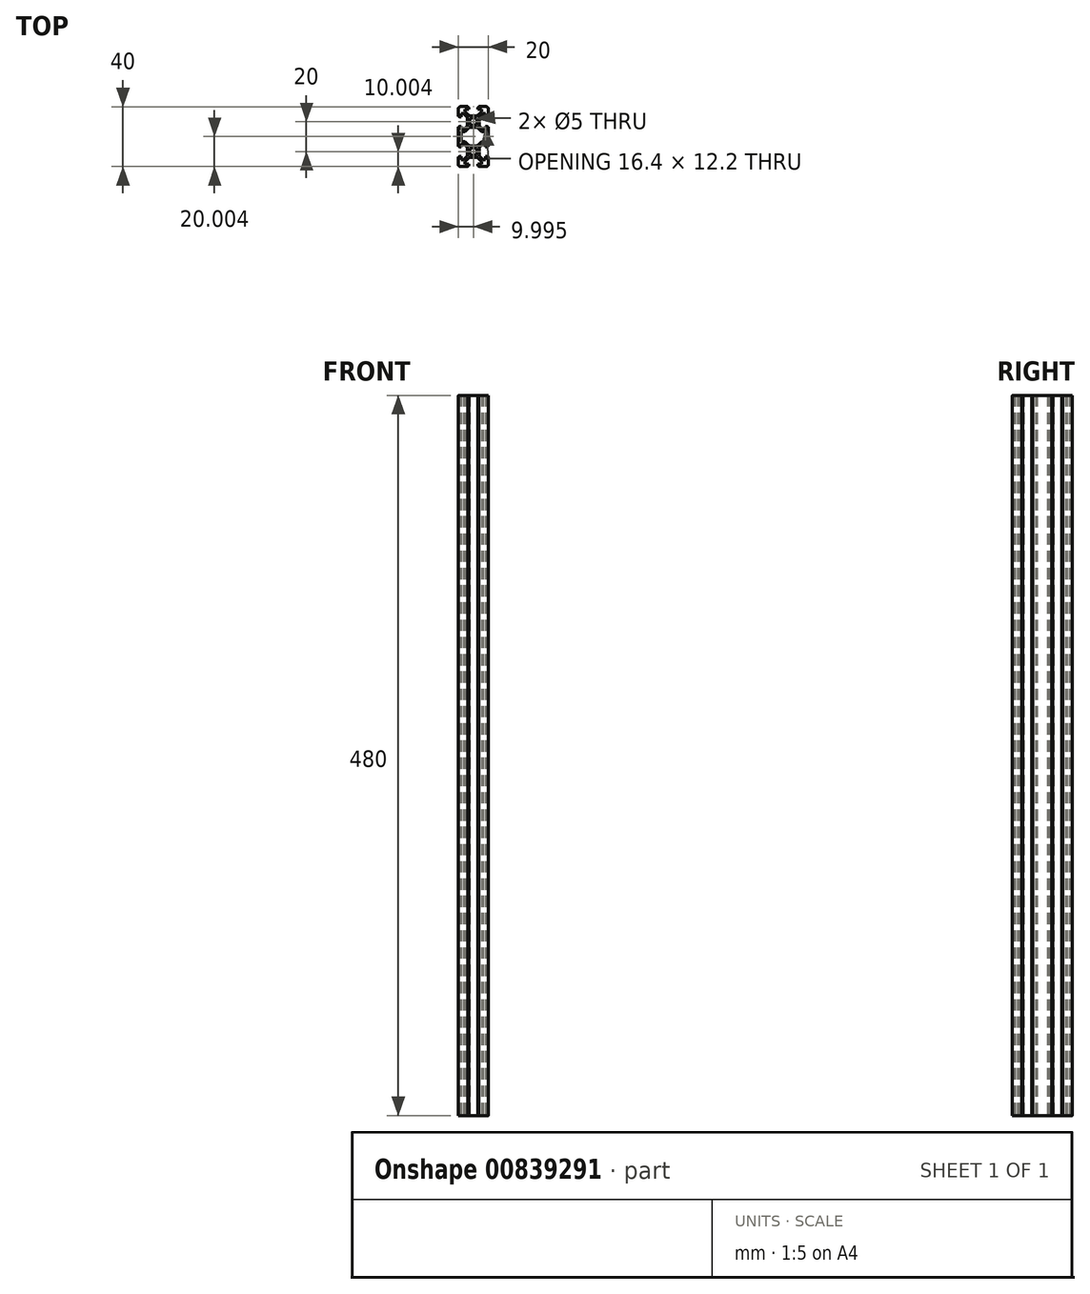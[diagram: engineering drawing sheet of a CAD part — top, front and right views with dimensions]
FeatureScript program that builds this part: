
annotation { "Feature Type Name" : "Feature", "Feature Type Description" : "" }
export const myFeature = defineFeature(function(context is Context, id is Id, definition is map)
    precondition{}
    {
        {
            var Q0;
            Q0=qCreatedBy(makeId("Top.planeOp"),FACE);
            var sketch = newSketch(context, id + "F0", { "sketchPlane" : qUnion([Q0])});
            skCircle(sketch, "E0", {"center": v(-160.4, -45.54) * mm, "radius": 2.5 * mm});
            skLineSegment(sketch, "E1.bottom", {"start": v(-151.9, -55.54) * mm, "end": v(-156.3, -55.54) * mm});
            skLineSegment(sketch, "E1.left", {"start": v(-150.4, -54.04) * mm, "end": v(-150.4, -49.14) * mm});
            skLineSegment(sketch, "E2.bottom", {"start": v(-158.38, -49.44) * mm, "end": v(-162.4, -49.44) * mm});
            skLineSegment(sketch, "E2.top", {"start": v(-158.38, -41.64) * mm, "end": v(-162.4, -41.64) * mm});
            skLineSegment(sketch, "E2.left", {"start": v(-156.5, -47.55) * mm, "end": v(-156.5, -43.52) * mm});
            skLineSegment(sketch, "E2.right", {"start": v(-164.3, -47.55) * mm, "end": v(-164.3, -43.52) * mm});
            skLineSegment(sketch, "E3.left", {"start": v(-150.4, -37.04) * mm, "end": v(-150.4, -40.04) * mm});
            skLineSegment(sketch, "E4", {"start": v(-155.9, -42.11) * mm, "end": v(-153.83, -40.04) * mm});
            skLineSegment(sketch, "E5.MirrorCS", {"start": v(-156.97, -41.05) * mm, "end": v(-154.9, -38.98) * mm});
            skLineSegment(sketch, "E6", {"start": v(-152.2, -40.04) * mm, "end": v(-152.2, -42.44) * mm});
            skLineSegment(sketch, "E7", {"start": v(-150.7, -41.94) * mm, "end": v(-150.4, -41.94) * mm});
            skLineSegment(sketch, "E8", {"start": v(-152.2, -42.44) * mm, "end": v(-150.9, -42.44) * mm});
            skLineSegment(sketch, "E9", {"start": v(-150.9, -42.14) * mm, "end": v(-150.9, -42.44) * mm});
            skPoint(sketch, "E10.visualSharp", {"position": v(-150.9, -41.94) * mm});
            skArc(sketch, "E10.filletArc", {"start": v(-150.7, -41.94) * mm, "mid": v(-150.84, -42) * mm, "end": v(-150.9, -42.14) * mm});
            skPoint(sketch, "E11.newPointA", {"position": v(-156.5, -42.7) * mm});
            skArc(sketch, "E11.filletArc", {"start": v(-155.9, -42.11) * mm, "mid": v(-156.34, -42.76) * mm, "end": v(-156.5, -43.52) * mm});
            skPoint(sketch, "E12.newPointA", {"position": v(-157.56, -41.64) * mm});
            skPoint(sketch, "E12.newPointB", {"position": v(-156.5, -41.64) * mm});
            skArc(sketch, "E12.filletArc", {"start": v(-158.38, -41.64) * mm, "mid": v(-157.62, -41.48) * mm, "end": v(-156.97, -41.05) * mm});
            skLineSegment(sketch, "E13.trimOffspring", {"start": v(-152.2, -40.04) * mm, "end": v(-153.83, -40.04) * mm});
            skLineSegment(sketch, "E14.MirrorCS", {"start": v(-150.7, -49.14) * mm, "end": v(-150.4, -49.14) * mm});
            skArc(sketch, "E15.MirrorCS", {"start": v(-150.7, -49.14) * mm, "mid": v(-150.84, -49.08) * mm, "end": v(-150.9, -48.94) * mm});
            skLineSegment(sketch, "E16.MirrorCS", {"start": v(-150.9, -48.94) * mm, "end": v(-150.9, -48.64) * mm});
            skArc(sketch, "E17.MirrorCS", {"start": v(-155.9, -48.96) * mm, "mid": v(-156.34, -48.31) * mm, "end": v(-156.5, -47.55) * mm});
            skLineSegment(sketch, "E18.MirrorCS", {"start": v(-152.2, -51.04) * mm, "end": v(-153.83, -51.04) * mm});
            skLineSegment(sketch, "E19.MirrorCS", {"start": v(-152.2, -48.64) * mm, "end": v(-150.9, -48.64) * mm});
            skLineSegment(sketch, "E20.MirrorCS", {"start": v(-151.9, -55.54) * mm, "end": v(-154.9, -55.54) * mm});
            skPoint(sketch, "E21.MirrorP", {"position": v(-150.9, -49.14) * mm});
            skLineSegment(sketch, "E22.MirrorCS", {"start": v(-157.3, -53.74) * mm, "end": v(-157.3, -55.04) * mm});
            skLineSegment(sketch, "E23.MirrorCS", {"start": v(-154.9, -53.74) * mm, "end": v(-157.3, -53.74) * mm});
            skLineSegment(sketch, "E24.MirrorCS", {"start": v(-152.2, -51.04) * mm, "end": v(-152.2, -48.64) * mm});
            skLineSegment(sketch, "E25.MirrorCS", {"start": v(-150.4, -54.04) * mm, "end": v(-150.4, -51.04) * mm});
            skLineSegment(sketch, "E26.MirrorCS", {"start": v(-155.9, -48.96) * mm, "end": v(-153.83, -51.04) * mm});
            skPoint(sketch, "E27.MirrorP", {"position": v(-156.5, -48.38) * mm});
            skPoint(sketch, "E28.MirrorP", {"position": v(-150.4, -55.54) * mm});
            skPoint(sketch, "E29.MirrorP", {"position": v(-156.5, -49.44) * mm});
            skLineSegment(sketch, "E30.MirrorCS", {"start": v(-156.97, -50.02) * mm, "end": v(-154.9, -52.1) * mm});
            skPoint(sketch, "E31.MirrorP", {"position": v(-157.56, -49.44) * mm});
            skArc(sketch, "E32.MirrorCS", {"start": v(-150.4, -54.04) * mm, "mid": v(-150.83, -55.1) * mm, "end": v(-151.9, -55.54) * mm});
            skLineSegment(sketch, "E33.MirrorCS", {"start": v(-154.9, -53.74) * mm, "end": v(-154.9, -52.1) * mm});
            skArc(sketch, "E34.MirrorCS", {"start": v(-158.38, -49.44) * mm, "mid": v(-157.62, -49.59) * mm, "end": v(-156.97, -50.02) * mm});
            skLineSegment(sketch, "E35.trimOffspring", {"start": v(-150.4, -41.94) * mm, "end": v(-150.4, -37.04) * mm});
            skLineSegment(sketch, "E36.MirrorCS", {"start": v(-156.8, -55.24) * mm, "end": v(-156.8, -55.54) * mm});
            skLineSegment(sketch, "E37.MirrorCS", {"start": v(-157, -55.04) * mm, "end": v(-157.3, -55.04) * mm});
            skLineSegment(sketch, "E38.MirrorCS", {"start": v(-156.3, -55.54) * mm, "end": v(-156.8, -55.54) * mm});
            skArc(sketch, "E39.MirrorCS", {"start": v(-156.8, -55.24) * mm, "mid": v(-156.85, -55.1) * mm, "end": v(-157, -55.04) * mm});
            skArc(sketch, "E40.MirrorCS", {"start": v(-170.1, -49.14) * mm, "mid": v(-169.95, -49.08) * mm, "end": v(-169.9, -48.94) * mm});
            skLineSegment(sketch, "E41.MirrorCS", {"start": v(-170.1, -41.94) * mm, "end": v(-170.4, -41.94) * mm});
            skLineSegment(sketch, "E42.MirrorCS", {"start": v(-169.9, -48.94) * mm, "end": v(-169.9, -48.64) * mm});
            skArc(sketch, "E43.MirrorCS", {"start": v(-170.1, -41.94) * mm, "mid": v(-169.95, -42) * mm, "end": v(-169.9, -42.14) * mm});
            skLineSegment(sketch, "E44.MirrorCS", {"start": v(-169.9, -42.14) * mm, "end": v(-169.9, -42.44) * mm});
            skLineSegment(sketch, "E45.MirrorCS", {"start": v(-170.1, -49.14) * mm, "end": v(-170.4, -49.14) * mm});
            skArc(sketch, "E46.MirrorCS", {"start": v(-170.4, -54.04) * mm, "mid": v(-169.96, -55.1) * mm, "end": v(-168.9, -55.54) * mm});
            skArc(sketch, "E47.MirrorCS", {"start": v(-164.88, -42.11) * mm, "mid": v(-164.45, -42.76) * mm, "end": v(-164.3, -43.52) * mm});
            skLineSegment(sketch, "E48.MirrorCS", {"start": v(-163.8, -55.04) * mm, "end": v(-163.5, -55.04) * mm});
            skLineSegment(sketch, "E49.MirrorCS", {"start": v(-162.4, -41.64) * mm, "end": v(-158.38, -41.64) * mm});
            skLineSegment(sketch, "E50.MirrorCS", {"start": v(-168.6, -48.64) * mm, "end": v(-169.9, -48.64) * mm});
            skLineSegment(sketch, "E51.MirrorCS", {"start": v(-168.6, -42.44) * mm, "end": v(-169.9, -42.44) * mm});
            skArc(sketch, "E52.MirrorCS", {"start": v(-164.88, -48.96) * mm, "mid": v(-164.45, -48.31) * mm, "end": v(-164.3, -47.55) * mm});
            skArc(sketch, "E53.MirrorCS", {"start": v(-164, -55.24) * mm, "mid": v(-163.94, -55.1) * mm, "end": v(-163.8, -55.04) * mm});
            skLineSegment(sketch, "E54.MirrorCS", {"start": v(-164, -55.24) * mm, "end": v(-164, -55.54) * mm});
            skLineSegment(sketch, "E55.MirrorCS", {"start": v(-162.4, -49.44) * mm, "end": v(-158.38, -49.44) * mm});
            skLineSegment(sketch, "E56.MirrorCS", {"start": v(-164.5, -55.54) * mm, "end": v(-164, -55.54) * mm});
            skLineSegment(sketch, "E57.MirrorCS", {"start": v(-163.5, -53.74) * mm, "end": v(-163.5, -55.04) * mm});
            skArc(sketch, "E58.MirrorCS", {"start": v(-162.4, -41.64) * mm, "mid": v(-163.17, -41.48) * mm, "end": v(-163.82, -41.05) * mm});
            skPoint(sketch, "E59.MirrorP", {"position": v(-170.4, -55.54) * mm});
            skLineSegment(sketch, "E60.MirrorCS", {"start": v(-168.9, -55.54) * mm, "end": v(-164.5, -55.54) * mm});
            skPoint(sketch, "E61.MirrorP", {"position": v(-164.3, -49.44) * mm});
            skArc(sketch, "E62.MirrorCS", {"start": v(-162.4, -49.44) * mm, "mid": v(-163.17, -49.59) * mm, "end": v(-163.82, -50.02) * mm});
            skPoint(sketch, "E63.MirrorP", {"position": v(-164.3, -48.38) * mm});
            skLineSegment(sketch, "E64.MirrorCS", {"start": v(-163.82, -41.05) * mm, "end": v(-165.9, -38.98) * mm});
            skPoint(sketch, "E65.MirrorP", {"position": v(-164.3, -42.7) * mm});
            skLineSegment(sketch, "E66.MirrorCS", {"start": v(-168.6, -51.04) * mm, "end": v(-168.6, -48.64) * mm});
            skLineSegment(sketch, "E67.MirrorCS", {"start": v(-164.88, -48.96) * mm, "end": v(-166.96, -51.04) * mm});
            skLineSegment(sketch, "E68.MirrorCS", {"start": v(-165.9, -53.74) * mm, "end": v(-163.5, -53.74) * mm});
            skLineSegment(sketch, "E69.MirrorCS", {"start": v(-168.6, -51.04) * mm, "end": v(-166.96, -51.04) * mm});
            skLineSegment(sketch, "E70.MirrorCS", {"start": v(-170.4, -54.04) * mm, "end": v(-170.4, -51.04) * mm});
            skLineSegment(sketch, "E71.MirrorCS", {"start": v(-170.4, -41.94) * mm, "end": v(-170.4, -37.04) * mm});
            skLineSegment(sketch, "E72.MirrorCS", {"start": v(-163.82, -50.02) * mm, "end": v(-165.9, -52.1) * mm});
            skPoint(sketch, "E73.MirrorP", {"position": v(-163.23, -49.44) * mm});
            skLineSegment(sketch, "E74.MirrorCS", {"start": v(-168.6, -40.04) * mm, "end": v(-168.6, -42.44) * mm});
            skLineSegment(sketch, "E75.MirrorCS", {"start": v(-170.4, -37.04) * mm, "end": v(-170.4, -40.04) * mm});
            skPoint(sketch, "E76.MirrorP", {"position": v(-169.9, -49.14) * mm});
            skPoint(sketch, "E77.MirrorP", {"position": v(-170.4, -35.54) * mm});
            skPoint(sketch, "E78.MirrorP", {"position": v(-169.9, -41.94) * mm});
            skLineSegment(sketch, "E79.MirrorCS", {"start": v(-164.88, -42.11) * mm, "end": v(-166.96, -40.04) * mm});
            skLineSegment(sketch, "E80.MirrorCS", {"start": v(-168.6, -40.04) * mm, "end": v(-166.96, -40.04) * mm});
            skLineSegment(sketch, "E81.MirrorCS", {"start": v(-170.4, -54.04) * mm, "end": v(-170.4, -49.14) * mm});
            skLineSegment(sketch, "E82.MirrorCS", {"start": v(-168.9, -55.54) * mm, "end": v(-165.9, -55.54) * mm});
            skPoint(sketch, "E83.MirrorP", {"position": v(-164.3, -41.64) * mm});
            skPoint(sketch, "E84.MirrorP", {"position": v(-163.23, -41.64) * mm});
            skLineSegment(sketch, "E85.MirrorCS", {"start": v(-165.9, -53.74) * mm, "end": v(-165.9, -52.1) * mm});
            skLineSegment(sketch, "E86", {"start": v(-168.6, -38.98) * mm, "end": v(-168.6, -35.54) * mm});
            skLineSegment(sketch, "E87", {"start": v(-170.4, -37.04) * mm, "end": v(-170.4, -35.54) * mm});
            skLineSegment(sketch, "E88", {"start": v(-150.4, -35.54) * mm, "end": v(-150.4, -37.04) * mm});
            skLineSegment(sketch, "E89", {"start": v(-152.2, -38.98) * mm, "end": v(-152.2, -35.54) * mm});
            skLineSegment(sketch, "E90", {"start": v(-154.9, -38.98) * mm, "end": v(-152.2, -38.98) * mm});
            skLineSegment(sketch, "E91", {"start": v(-165.9, -38.98) * mm, "end": v(-168.6, -38.98) * mm});
            skLineSegment(sketch, "E92.MirrorCS", {"start": v(-150.7, -21.94) * mm, "end": v(-150.4, -21.94) * mm});
            skLineSegment(sketch, "E93.MirrorCS", {"start": v(-150.9, -22.14) * mm, "end": v(-150.9, -22.44) * mm});
            skArc(sketch, "E94.MirrorCS", {"start": v(-150.7, -21.94) * mm, "mid": v(-150.84, -22) * mm, "end": v(-150.9, -22.14) * mm});
            skArc(sketch, "E95.MirrorCS", {"start": v(-150.7, -29.14) * mm, "mid": v(-150.84, -29.08) * mm, "end": v(-150.9, -28.94) * mm});
            skLineSegment(sketch, "E96.MirrorCS", {"start": v(-150.9, -28.94) * mm, "end": v(-150.9, -28.64) * mm});
            skLineSegment(sketch, "E97.MirrorCS", {"start": v(-169.9, -22.14) * mm, "end": v(-169.9, -22.44) * mm});
            skLineSegment(sketch, "E98.MirrorCS", {"start": v(-150.7, -29.14) * mm, "end": v(-150.4, -29.14) * mm});
            skArc(sketch, "E99.MirrorCS", {"start": v(-170.1, -21.94) * mm, "mid": v(-169.95, -22) * mm, "end": v(-169.9, -22.14) * mm});
            skLineSegment(sketch, "E100.MirrorCS", {"start": v(-170.1, -21.94) * mm, "end": v(-170.4, -21.94) * mm});
            skLineSegment(sketch, "E101.MirrorCS", {"start": v(-169.9, -28.94) * mm, "end": v(-169.9, -28.64) * mm});
            skArc(sketch, "E102.MirrorCS", {"start": v(-170.1, -29.14) * mm, "mid": v(-169.95, -29.08) * mm, "end": v(-169.9, -28.94) * mm});
            skLineSegment(sketch, "E103.MirrorCS", {"start": v(-170.1, -29.14) * mm, "end": v(-170.4, -29.14) * mm});
            skArc(sketch, "E104.MirrorCS", {"start": v(-158.38, -21.64) * mm, "mid": v(-157.62, -21.48) * mm, "end": v(-156.97, -21.05) * mm});
            skLineSegment(sketch, "E105.MirrorCS", {"start": v(-156.8, -15.84) * mm, "end": v(-156.8, -15.54) * mm});
            skArc(sketch, "E106.MirrorCS", {"start": v(-158.38, -29.44) * mm, "mid": v(-157.62, -29.59) * mm, "end": v(-156.97, -30.02) * mm});
            skLineSegment(sketch, "E107.MirrorCS", {"start": v(-152.2, -31.04) * mm, "end": v(-153.83, -31.04) * mm});
            skLineSegment(sketch, "E108.MirrorCS", {"start": v(-163.8, -16.04) * mm, "end": v(-163.5, -16.04) * mm});
            skLineSegment(sketch, "E109.MirrorCS", {"start": v(-168.6, -20.04) * mm, "end": v(-166.96, -20.04) * mm});
            skArc(sketch, "E110.MirrorCS", {"start": v(-170.4, -17.04) * mm, "mid": v(-169.96, -15.98) * mm, "end": v(-168.9, -15.54) * mm});
            skLineSegment(sketch, "E111.MirrorCS", {"start": v(-152.2, -28.64) * mm, "end": v(-150.9, -28.64) * mm});
            skLineSegment(sketch, "E112.MirrorCS", {"start": v(-164.5, -15.54) * mm, "end": v(-164, -15.54) * mm});
            skArc(sketch, "E113.MirrorCS", {"start": v(-164.88, -22.11) * mm, "mid": v(-164.45, -22.76) * mm, "end": v(-164.3, -23.52) * mm});
            skArc(sketch, "E114.MirrorCS", {"start": v(-150.4, -17.04) * mm, "mid": v(-150.83, -15.98) * mm, "end": v(-151.9, -15.54) * mm});
            skArc(sketch, "E115.MirrorCS", {"start": v(-162.4, -29.44) * mm, "mid": v(-163.17, -29.59) * mm, "end": v(-163.82, -30.02) * mm});
            skLineSegment(sketch, "E116.MirrorCS", {"start": v(-168.6, -22.44) * mm, "end": v(-169.9, -22.44) * mm});
            skLineSegment(sketch, "E117.MirrorCS", {"start": v(-164, -15.84) * mm, "end": v(-164, -15.54) * mm});
            skLineSegment(sketch, "E118.MirrorCS", {"start": v(-157.3, -17.34) * mm, "end": v(-157.3, -16.04) * mm});
            skLineSegment(sketch, "E119.MirrorCS", {"start": v(-156.3, -15.54) * mm, "end": v(-156.8, -15.54) * mm});
            skLineSegment(sketch, "E120.MirrorCS", {"start": v(-163.5, -17.34) * mm, "end": v(-163.5, -16.04) * mm});
            skArc(sketch, "E121.MirrorCS", {"start": v(-155.9, -28.96) * mm, "mid": v(-156.34, -28.31) * mm, "end": v(-156.5, -27.55) * mm});
            skArc(sketch, "E122.MirrorCS", {"start": v(-164.88, -28.96) * mm, "mid": v(-164.45, -28.31) * mm, "end": v(-164.3, -27.55) * mm});
            skLineSegment(sketch, "E123.MirrorCS", {"start": v(-152.2, -22.44) * mm, "end": v(-150.9, -22.44) * mm});
            skLineSegment(sketch, "E124.MirrorCS", {"start": v(-152.2, -20.04) * mm, "end": v(-153.83, -20.04) * mm});
            skArc(sketch, "E125.MirrorCS", {"start": v(-164, -15.84) * mm, "mid": v(-163.94, -15.98) * mm, "end": v(-163.8, -16.04) * mm});
            skLineSegment(sketch, "E126.MirrorCS", {"start": v(-157, -16.04) * mm, "end": v(-157.3, -16.04) * mm});
            skLineSegment(sketch, "E127.MirrorCS", {"start": v(-168.6, -31.04) * mm, "end": v(-166.96, -31.04) * mm});
            skLineSegment(sketch, "E128.MirrorCS", {"start": v(-168.6, -28.64) * mm, "end": v(-169.9, -28.64) * mm});
            skLineSegment(sketch, "E129.MirrorCS", {"start": v(-154.9, -17.34) * mm, "end": v(-154.9, -18.98) * mm});
            skLineSegment(sketch, "E130.MirrorCS", {"start": v(-165.9, -17.34) * mm, "end": v(-165.9, -18.98) * mm});
            skArc(sketch, "E131.MirrorCS", {"start": v(-162.4, -21.64) * mm, "mid": v(-163.17, -21.48) * mm, "end": v(-163.82, -21.05) * mm});
            skArc(sketch, "E132.MirrorCS", {"start": v(-155.9, -22.11) * mm, "mid": v(-156.34, -22.76) * mm, "end": v(-156.5, -23.52) * mm});
            skArc(sketch, "E133.MirrorCS", {"start": v(-156.8, -15.84) * mm, "mid": v(-156.85, -15.98) * mm, "end": v(-157, -16.04) * mm});
            skPoint(sketch, "E134.MirrorP", {"position": v(-160.4, -25.54) * mm});
            skLineSegment(sketch, "E135.MirrorCS", {"start": v(-164.3, -23.52) * mm, "end": v(-164.3, -27.55) * mm});
            skPoint(sketch, "E136.MirrorP", {"position": v(-164.3, -21.64) * mm});
            skLineSegment(sketch, "E137.MirrorCS", {"start": v(-151.9, -15.54) * mm, "end": v(-154.9, -15.54) * mm});
            skLineSegment(sketch, "E138.MirrorCS", {"start": v(-158.38, -29.44) * mm, "end": v(-162.4, -29.44) * mm});
            skLineSegment(sketch, "E139.MirrorCS", {"start": v(-170.4, -17.04) * mm, "end": v(-170.4, -21.94) * mm});
            skLineSegment(sketch, "E140.MirrorCS", {"start": v(-150.4, -34.04) * mm, "end": v(-150.4, -31.04) * mm});
            skPoint(sketch, "E141.MirrorP", {"position": v(-156.5, -21.64) * mm});
            skLineSegment(sketch, "E142.MirrorCS", {"start": v(-168.9, -15.54) * mm, "end": v(-164.5, -15.54) * mm});
            skLineSegment(sketch, "E143.MirrorCS", {"start": v(-150.4, -17.04) * mm, "end": v(-150.4, -20.04) * mm});
            skLineSegment(sketch, "E144.MirrorCS", {"start": v(-158.38, -21.64) * mm, "end": v(-162.4, -21.64) * mm});
            skPoint(sketch, "E145.MirrorP", {"position": v(-170.4, -15.54) * mm});
            skLineSegment(sketch, "E146.MirrorCS", {"start": v(-170.4, -34.04) * mm, "end": v(-170.4, -31.04) * mm});
            skCircle(sketch, "E147.MirrorC", {"center": v(-160.4, -25.54) * mm, "radius": 2.5 * mm});
            skPoint(sketch, "E148.MirrorP", {"position": v(-150.4, -15.54) * mm});
            skPoint(sketch, "E149.MirrorP", {"position": v(-169.9, -21.94) * mm});
            skLineSegment(sketch, "E150.MirrorCS", {"start": v(-152.2, -20.04) * mm, "end": v(-152.2, -22.44) * mm});
            skPoint(sketch, "E151.MirrorP", {"position": v(-169.9, -29.14) * mm});
            skPoint(sketch, "E152.MirrorP", {"position": v(-157.56, -21.64) * mm});
            skLineSegment(sketch, "E153.MirrorCS", {"start": v(-163.82, -21.05) * mm, "end": v(-165.9, -18.98) * mm});
            skLineSegment(sketch, "E154.MirrorCS", {"start": v(-165.9, -17.34) * mm, "end": v(-163.5, -17.34) * mm});
            skPoint(sketch, "E155.MirrorP", {"position": v(-156.5, -28.38) * mm});
            skLineSegment(sketch, "E156.MirrorCS", {"start": v(-170.4, -17.04) * mm, "end": v(-170.4, -20.04) * mm});
            skPoint(sketch, "E157.MirrorP", {"position": v(-150.9, -29.14) * mm});
            skLineSegment(sketch, "E158.MirrorCS", {"start": v(-154.9, -32.1) * mm, "end": v(-152.2, -32.1) * mm});
            skLineSegment(sketch, "E159.MirrorCS", {"start": v(-155.9, -22.11) * mm, "end": v(-153.83, -20.04) * mm});
            skLineSegment(sketch, "E160.MirrorCS", {"start": v(-165.9, -32.1) * mm, "end": v(-168.6, -32.1) * mm});
            skLineSegment(sketch, "E161.MirrorCS", {"start": v(-154.9, -17.34) * mm, "end": v(-157.3, -17.34) * mm});
            skLineSegment(sketch, "E162.MirrorCS", {"start": v(-168.6, -20.04) * mm, "end": v(-168.6, -22.44) * mm});
            skPoint(sketch, "E163.MirrorP", {"position": v(-164.3, -22.7) * mm});
            skPoint(sketch, "E164.MirrorP", {"position": v(-156.5, -29.44) * mm});
            skLineSegment(sketch, "E165.MirrorCS", {"start": v(-162.4, -21.64) * mm, "end": v(-158.38, -21.64) * mm});
            skLineSegment(sketch, "E166.MirrorCS", {"start": v(-168.9, -15.54) * mm, "end": v(-165.9, -15.54) * mm});
            skPoint(sketch, "E167.MirrorP", {"position": v(-163.23, -29.44) * mm});
            skLineSegment(sketch, "E168.MirrorCS", {"start": v(-162.4, -29.44) * mm, "end": v(-158.38, -29.44) * mm});
            skPoint(sketch, "E169.MirrorP", {"position": v(-164.3, -28.38) * mm});
            skLineSegment(sketch, "E170.MirrorCS", {"start": v(-150.4, -17.04) * mm, "end": v(-150.4, -21.94) * mm});
            skPoint(sketch, "E171.MirrorP", {"position": v(-156.5, -22.7) * mm});
            skLineSegment(sketch, "E172.MirrorCS", {"start": v(-164.88, -22.11) * mm, "end": v(-166.96, -20.04) * mm});
            skPoint(sketch, "E173.MirrorP", {"position": v(-163.23, -21.64) * mm});
            skLineSegment(sketch, "E174.MirrorCS", {"start": v(-155.9, -28.96) * mm, "end": v(-153.83, -31.04) * mm});
            skLineSegment(sketch, "E175.MirrorCS", {"start": v(-156.97, -21.05) * mm, "end": v(-154.9, -18.98) * mm});
            skLineSegment(sketch, "E176.MirrorCS", {"start": v(-170.4, -29.14) * mm, "end": v(-170.4, -34.04) * mm});
            skPoint(sketch, "E177.MirrorP", {"position": v(-164.3, -29.44) * mm});
            skLineSegment(sketch, "E178.MirrorCS", {"start": v(-156.97, -30.02) * mm, "end": v(-154.9, -32.1) * mm});
            skLineSegment(sketch, "E179.MirrorCS", {"start": v(-168.6, -31.04) * mm, "end": v(-168.6, -28.64) * mm});
            skPoint(sketch, "E180.MirrorP", {"position": v(-157.56, -29.44) * mm});
            skLineSegment(sketch, "E181.MirrorCS", {"start": v(-163.82, -30.02) * mm, "end": v(-165.9, -32.1) * mm});
            skLineSegment(sketch, "E182.MirrorCS", {"start": v(-152.2, -31.04) * mm, "end": v(-152.2, -28.64) * mm});
            skPoint(sketch, "E183.MirrorP", {"position": v(-150.9, -21.94) * mm});
            skLineSegment(sketch, "E184.MirrorCS", {"start": v(-150.4, -29.14) * mm, "end": v(-150.4, -34.04) * mm});
            skLineSegment(sketch, "E185.MirrorCS", {"start": v(-164.88, -28.96) * mm, "end": v(-166.96, -31.04) * mm});
            skLineSegment(sketch, "E186.MirrorCS", {"start": v(-156.5, -23.52) * mm, "end": v(-156.5, -27.55) * mm});
            skLineSegment(sketch, "E187.MirrorCS", {"start": v(-151.9, -15.54) * mm, "end": v(-156.3, -15.54) * mm});
            skLineSegment(sketch, "E188.MirrorCS", {"start": v(-152.2, -32.1) * mm, "end": v(-152.2, -35.54) * mm});
            skLineSegment(sketch, "E189.MirrorCS", {"start": v(-150.4, -35.54) * mm, "end": v(-150.4, -34.04) * mm});
            skLineSegment(sketch, "E190.MirrorCS", {"start": v(-168.6, -32.1) * mm, "end": v(-168.6, -35.54) * mm});
            skLineSegment(sketch, "E191.MirrorCS", {"start": v(-170.4, -34.04) * mm, "end": v(-170.4, -35.54) * mm});
            skSolve(sketch);
        }
        {
            var Q0;
            Q0=makeQuery(id+"F0.imprint","IMPRINT",FACE,{"disambiguationData":[TD([[makeQuery(id+"F0.imprint","IMPRINT",EDGE,{"derivedFrom":sQuery(id+"F0.wireOp",EDGE,"E1.bottom")}),-1.0]])]});
            extrude(context, id + "F1", {"entities" : qUnion([Q0]), "depth" : 480 * mm, "offsetDistance" : 25 * mm});
        }
    });
